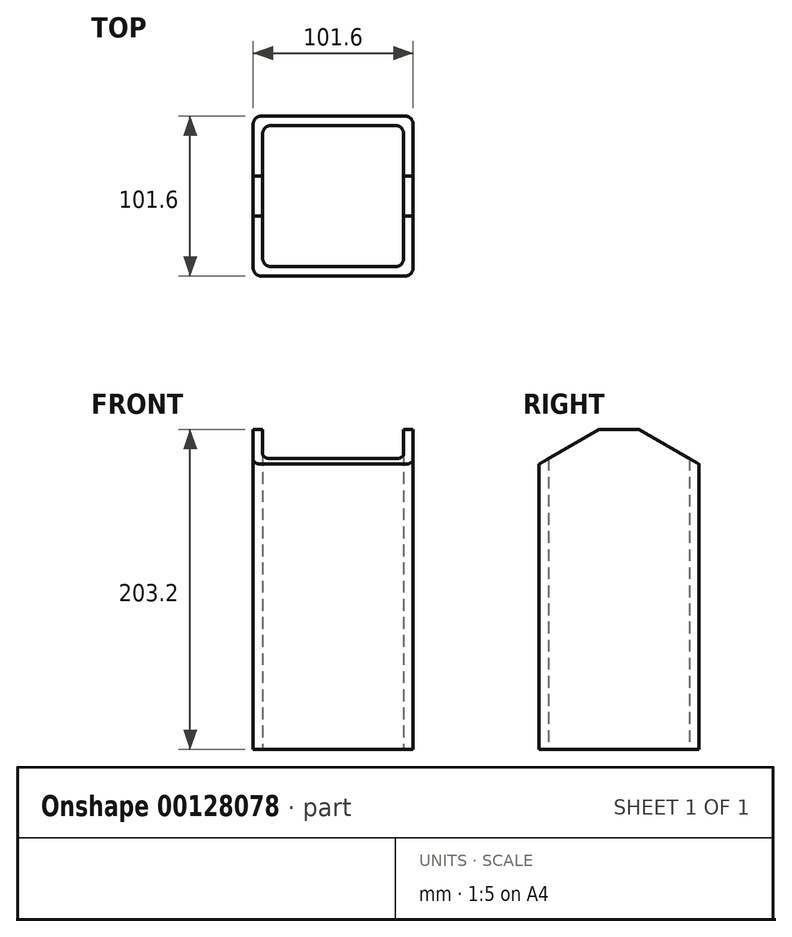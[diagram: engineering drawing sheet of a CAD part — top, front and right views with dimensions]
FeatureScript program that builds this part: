
annotation { "Feature Type Name" : "Feature", "Feature Type Description" : "" }
export const myFeature = defineFeature(function(context is Context, id is Id, definition is map)
    precondition{}
    {
        {
            var Q0;
            Q0=qCreatedBy(makeId("Top.planeOp"),FACE);
            var sketch = newSketch(context, id + "F0", { "sketchPlane" : qUnion([Q0])});
            skLineSegment(sketch, "E0", {"start": v(-50.8, 50.8) * mm, "end": v(-50.8, 0) * mm});
            skLineSegment(sketch, "E1", {"start": v(-50.8, 50.8) * mm, "end": v(0, 50.8) * mm});
            skLineSegment(sketch, "E2.MirrorCS", {"start": v(50.8, 50.8) * mm, "end": v(0, 50.8) * mm});
            skLineSegment(sketch, "E3.MirrorCS", {"start": v(50.8, 50.8) * mm, "end": v(50.8, 0) * mm});
            skLineSegment(sketch, "E4.MirrorCS", {"start": v(-50.8, -50.8) * mm, "end": v(-50.8, 0) * mm});
            skLineSegment(sketch, "E5.MirrorCS", {"start": v(-50.8, -50.8) * mm, "end": v(0, -50.8) * mm});
            skLineSegment(sketch, "E6.MirrorCS", {"start": v(50.8, -50.8) * mm, "end": v(0, -50.8) * mm});
            skLineSegment(sketch, "E7.MirrorCS", {"start": v(50.8, -50.8) * mm, "end": v(50.8, 0) * mm});
            skLineSegment(sketch, "E8.bottom", {"start": v(-44.78, 44.78) * mm, "end": v(44.78, 44.78) * mm});
            skLineSegment(sketch, "E8.top", {"start": v(-44.78, -44.78) * mm, "end": v(44.78, -44.78) * mm});
            skLineSegment(sketch, "E8.left", {"start": v(-44.78, 44.78) * mm, "end": v(-44.78, -44.78) * mm});
            skLineSegment(sketch, "E8.right", {"start": v(44.78, 44.78) * mm, "end": v(44.78, -44.78) * mm});
            skSolve(sketch);
        }
        {
            var Q0;
            Q0 = qSketchRegion(id + "F0", true);
            extrude(context, id + "F1", {"entities" : qUnion([Q0]), "depth" : 203.2 * mm});
        }
        {
            var Q0;
            Q0=makeQuery(id+"F1.opExtrude","SWEPT_FACE",FACE,{"disambiguationData":[OSD([sQuery(id+"F0.wireOp",EDGE,"E3.MirrorCS"),sQuery(id+"F0.wireOp",EDGE,"E7.MirrorCS")])]});
            var sketch = newSketch(context, id + "F2", { "sketchPlane" : qUnion([Q0])});
            skLineSegment(sketch, "E9", {"start": v(-50.8, 203.2) * mm, "end": v(-50.8, 181.2) * mm});
            skLineSegment(sketch, "E10", {"start": v(-50.8, 181.2) * mm, "end": v(-12.7, 203.2) * mm});
            skLineSegment(sketch, "E11", {"start": v(-12.7, 203.2) * mm, "end": v(-50.8, 203.2) * mm});
            skLineSegment(sketch, "E12", {"start": v(12.7, 203.2) * mm, "end": v(50.8, 203.2) * mm});
            skLineSegment(sketch, "E13", {"start": v(50.8, 203.2) * mm, "end": v(50.8, 181.2) * mm});
            skLineSegment(sketch, "E14", {"start": v(50.8, 181.2) * mm, "end": v(12.7, 203.2) * mm});
            skSolve(sketch);
        }
        {
            var Q0;
            Q0 = qSketchRegion(id + "F2", true);
            extrude(context, id + "F3", {"entities" : qUnion([Q0]), "operationType" : NewBodyOperationType.REMOVE, "oppositeDirection" : true, "depth" : 101.6 * mm});
        }
        {
            var Q0;
            Q0=makeQuery(id+"F1.opExtrude","SWEPT_EDGE",EDGE,{"disambiguationData":[OSD([sQuery(id+"F0.wireOp",EDGE,"E4.MirrorCS"),sQuery(id+"F0.wireOp",EDGE,"E5.MirrorCS")])]});
            var Q1;
            Q1=makeQuery(id+"F1.opExtrude","SWEPT_EDGE",EDGE,{"disambiguationData":[OSD([sQuery(id+"F0.wireOp",EDGE,"E6.MirrorCS"),sQuery(id+"F0.wireOp",EDGE,"E7.MirrorCS")])]});
            var Q2;
            Q2=makeQuery(id+"F1.opExtrude","SWEPT_EDGE",EDGE,{"disambiguationData":[OSD([sQuery(id+"F0.wireOp",EDGE,"E2.MirrorCS"),sQuery(id+"F0.wireOp",EDGE,"E3.MirrorCS")])]});
            var Q3;
            Q3=makeQuery(id+"F1.opExtrude","SWEPT_EDGE",EDGE,{"disambiguationData":[OSD([sQuery(id+"F0.wireOp",EDGE,"E8.bottom"),sQuery(id+"F0.wireOp",EDGE,"E8.left")])]});
            var Q4;
            Q4=makeQuery(id+"F1.opExtrude","SWEPT_EDGE",EDGE,{"disambiguationData":[OSD([sQuery(id+"F0.wireOp",EDGE,"E8.top"),sQuery(id+"F0.wireOp",EDGE,"E8.left")])]});
            var Q5;
            Q5=makeQuery(id+"F1.opExtrude","SWEPT_EDGE",EDGE,{"disambiguationData":[OSD([sQuery(id+"F0.wireOp",EDGE,"E0"),sQuery(id+"F0.wireOp",EDGE,"E1")])]});
            var Q6;
            Q6=makeQuery(id+"F1.opExtrude","SWEPT_EDGE",EDGE,{"disambiguationData":[OSD([sQuery(id+"F0.wireOp",EDGE,"E8.top"),sQuery(id+"F0.wireOp",EDGE,"E8.right")])]});
            var Q7;
            Q7=makeQuery(id+"F1.opExtrude","SWEPT_EDGE",EDGE,{"disambiguationData":[OSD([sQuery(id+"F0.wireOp",EDGE,"E8.bottom"),sQuery(id+"F0.wireOp",EDGE,"E8.right")])]});
            fillet(context, id + "F4", {"entities" : qUnion([Q0, Q1, Q2, Q3, Q4, Q5, Q6, Q7]), "radius" : 5.08 * mm, "tangentPropagation" : true, "allowEdgeOverflow" : false});
        }
    });
